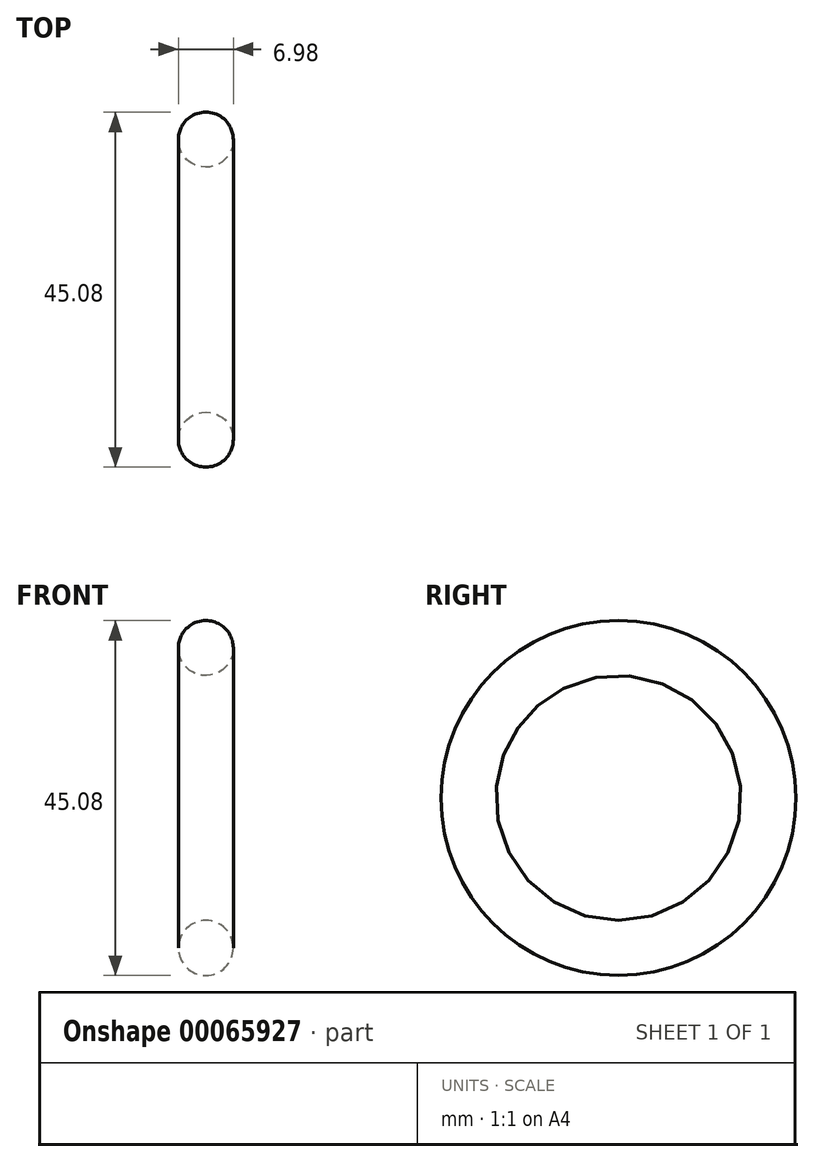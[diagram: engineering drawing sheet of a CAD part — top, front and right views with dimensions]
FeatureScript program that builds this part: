
annotation { "Feature Type Name" : "Feature", "Feature Type Description" : "" }
export const myFeature = defineFeature(function(context is Context, id is Id, definition is map)
    precondition{}
    {
        {
            var Q0;
            Q0=qCreatedBy(makeId("Front.planeOp"),FACE);
            var sketch = newSketch(context, id + "F0", { "sketchPlane" : qUnion([Q0])});
            skLineSegment(sketch, "E0", {"start": v(0, 0) * mm, "end": v(-6.06, 0) * mm, "construction": true});
            skCircle(sketch, "E1", {"center": v(0, 19.05) * mm, "radius": 3.5 * mm});
            skSolve(sketch);
        }
        {
            var Q0;
            Q0=makeQuery(id+"F0.imprint","IMPRINT",FACE,{"disambiguationData":[TD([[makeQuery(id+"F0.imprint","IMPRINT",EDGE,{"derivedFrom":sQuery(id+"F0.wireOp",EDGE,"E1")}),1.0]])]});
            var Q1;
            Q1=sQuery(id+"F0.wireOp",EDGE,"E0");
            revolve(context, id + "F1", {"entities" : qUnion([Q0]), "axis" : qUnion([Q1]), "revolveType" : RevolveType.FULL});
        }
    });
